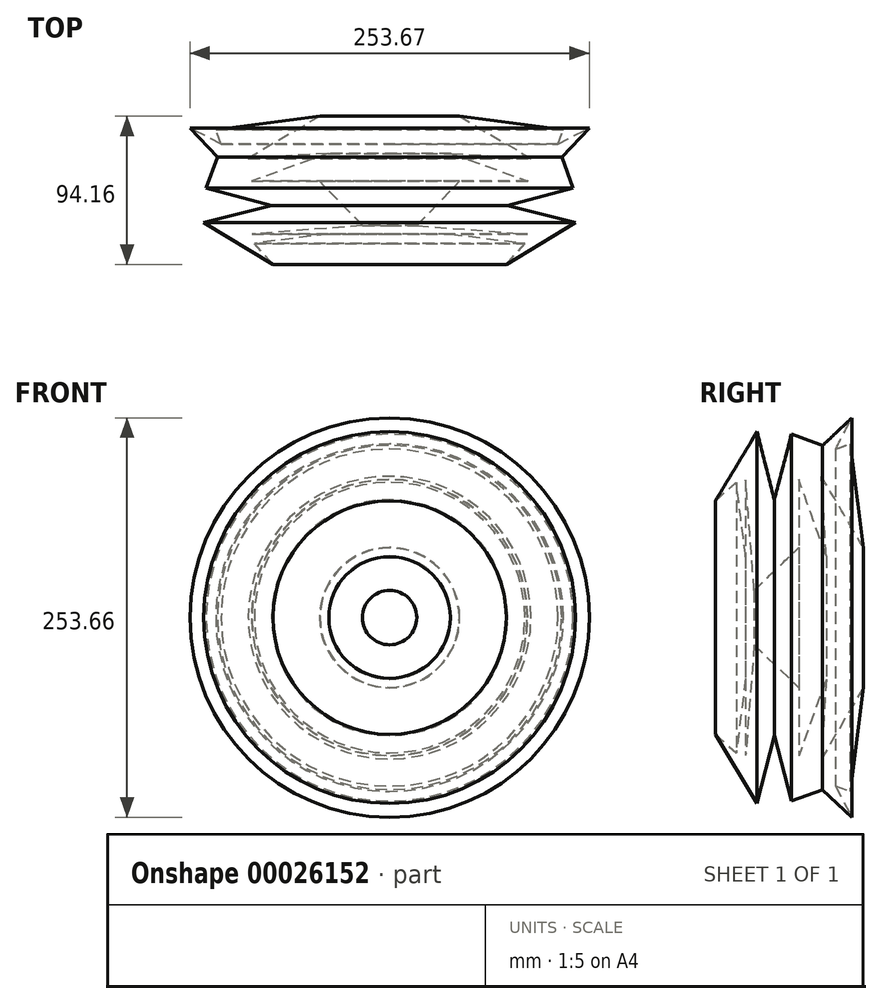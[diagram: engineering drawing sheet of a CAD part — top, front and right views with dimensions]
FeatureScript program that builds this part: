
annotation { "Feature Type Name" : "Feature", "Feature Type Description" : "" }
export const myFeature = defineFeature(function(context is Context, id is Id, definition is map)
    precondition{}
    {
        {
            var Q0;
            Q0=qCreatedBy(makeId("Top.planeOp"),FACE);
            var sketch = newSketch(context, id + "F0", { "sketchPlane" : qUnion([Q0])});
            skLineSegment(sketch, "E0", {"start": v(39.1, 51.97) * mm, "end": v(-27.01, 60.46) * mm});
            skLineSegment(sketch, "E1", {"start": v(-27.01, 60.46) * mm, "end": v(18.52, 33.7) * mm});
            skLineSegment(sketch, "E2", {"start": v(18.52, 33.7) * mm, "end": v(-32.16, 36.79) * mm});
            skLineSegment(sketch, "E3", {"start": v(-32.16, 36.79) * mm, "end": v(16.47, 19.3) * mm});
            skLineSegment(sketch, "E4", {"start": v(16.47, 19.3) * mm, "end": v(-26.76, 19.3) * mm});
            skLineSegment(sketch, "E5", {"start": v(-26.76, 19.3) * mm, "end": v(-54.03, -9) * mm});
            skLineSegment(sketch, "E6", {"start": v(-54.03, -9) * mm, "end": v(16.2, -14.4) * mm});
            skLineSegment(sketch, "E7", {"start": v(16.2, -14.4) * mm, "end": v(-32.67, -14.4) * mm});
            skLineSegment(sketch, "E8", {"start": v(-32.67, -14.4) * mm, "end": v(14.66, -20.32) * mm});
            skLineSegment(sketch, "E9", {"start": v(14.66, -20.32) * mm, "end": v(2.83, -33.7) * mm});
            skLineSegment(sketch, "E10", {"start": v(2.83, -33.7) * mm, "end": v(46.82, -7.2) * mm});
            skLineSegment(sketch, "E11", {"start": v(46.82, -7.2) * mm, "end": v(3.6, 3.86) * mm});
            skLineSegment(sketch, "E12", {"start": v(3.6, 3.86) * mm, "end": v(45.28, 14.66) * mm});
            skLineSegment(sketch, "E13", {"start": v(45.28, 14.66) * mm, "end": v(38.08, 34.47) * mm});
            skLineSegment(sketch, "E14", {"start": v(38.08, 34.47) * mm, "end": v(55.57, 53) * mm});
            skLineSegment(sketch, "E15", {"start": v(55.57, 53) * mm, "end": v(35.76, 42.7) * mm});
            skLineSegment(sketch, "E16", {"start": v(35.76, 42.7) * mm, "end": v(39.1, 51.97) * mm});
            skSolve(sketch);
        }
        {
            var Q0;
            Q0=qCreatedBy(makeId("Top.planeOp"),FACE);
            var sketch = newSketch(context, id + "F1", { "sketchPlane" : qUnion([Q0])});
            skLineSegment(sketch, "E17", {"start": v(-71.26, 53.25) * mm, "end": v(-71.26, -44.5) * mm});
            skSolve(sketch);
        }
        {
            var Q0;
            Q0=makeQuery(id+"F0.imprint","IMPRINT",FACE,{"disambiguationData":[TD([[makeQuery(id+"F0.imprint","IMPRINT",EDGE,{"derivedFrom":sQuery(id+"F0.wireOp",EDGE,"E0")}),1.0]])]});
            var Q1;
            Q1=sQuery(id+"F1.wireOp",EDGE,"E17");
            revolve(context, id + "F2", {"entities" : qUnion([Q0]), "axis" : qUnion([Q1]), "revolveType" : RevolveType.FULL});
        }
    });
